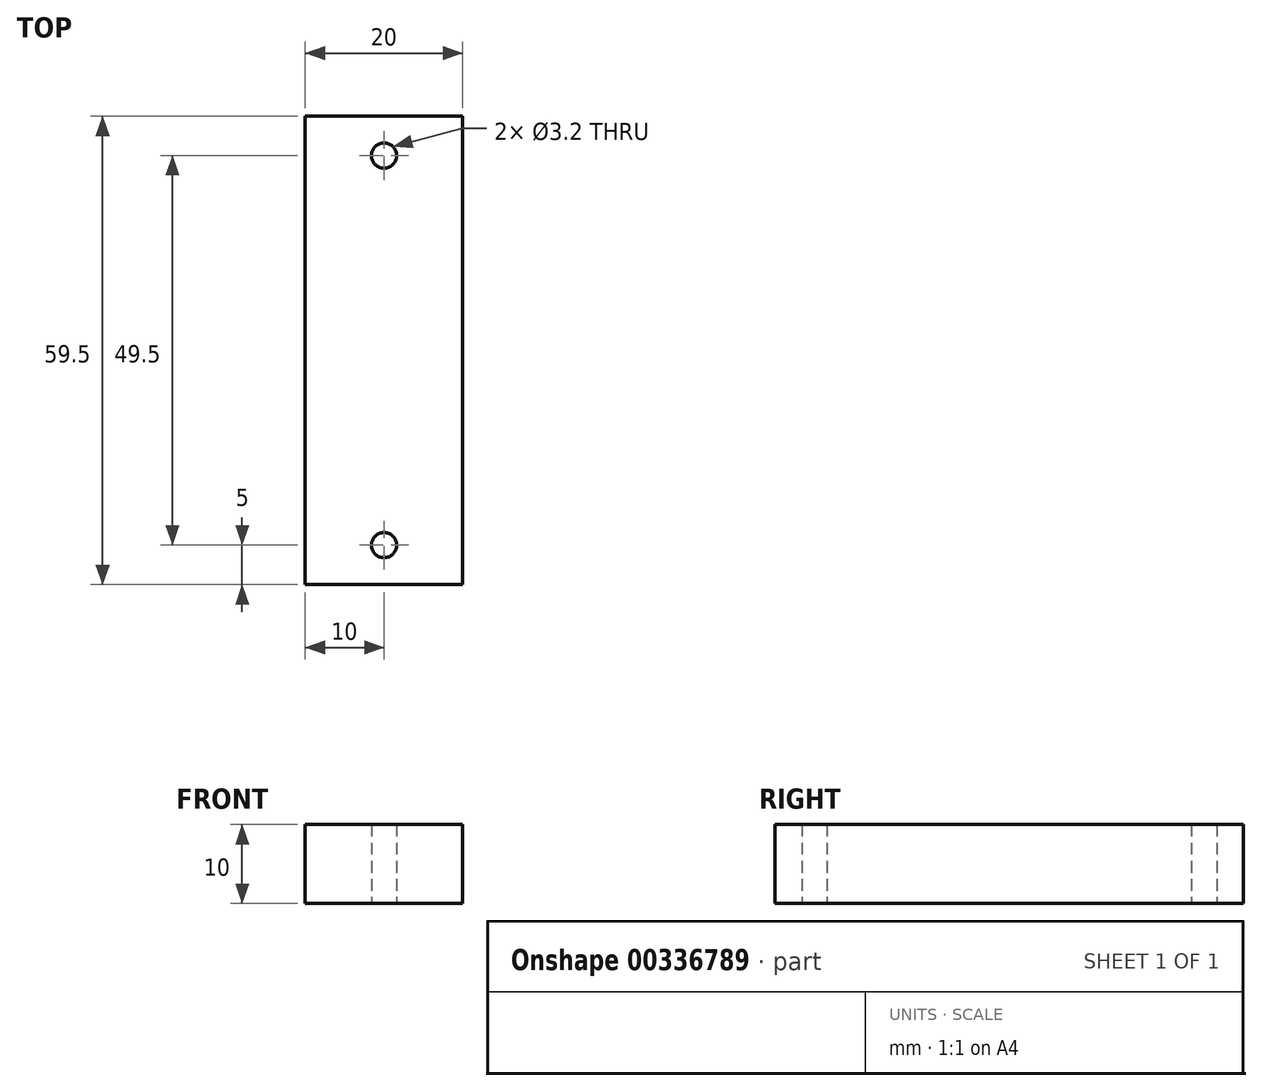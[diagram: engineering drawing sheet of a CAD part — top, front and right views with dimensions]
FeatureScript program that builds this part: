
annotation { "Feature Type Name" : "Feature", "Feature Type Description" : "" }
export const myFeature = defineFeature(function(context is Context, id is Id, definition is map)
    precondition{}
    {
        {
            var Q0;
            Q0=qCreatedBy(makeId("Top.planeOp"),FACE);
            var sketch = newSketch(context, id + "F0", { "sketchPlane" : qUnion([Q0])});
            skLineSegment(sketch, "E0.bottom", {"start": v(10, 29.75) * mm, "end": v(-10, 29.75) * mm});
            skLineSegment(sketch, "E0.top", {"start": v(10, -29.75) * mm, "end": v(-10, -29.75) * mm});
            skLineSegment(sketch, "E0.left", {"start": v(10, 29.75) * mm, "end": v(10, -29.75) * mm});
            skLineSegment(sketch, "E0.right", {"start": v(-10, 29.75) * mm, "end": v(-10, -29.75) * mm});
            skPoint(sketch, "E0.middle", {"position": v(0, 0) * mm});
            skPoint(sketch, "E1", {"position": v(0, 24.75) * mm});
            skCircle(sketch, "E2", {"center": v(0, 24.75) * mm, "radius": 1.6 * mm});
            skCircle(sketch, "E3.MirrorC", {"center": v(0, -24.75) * mm, "radius": 1.6 * mm});
            skSolve(sketch);
        }
        {
            var Q0;
            Q0=makeQuery(id+"F0.imprint","IMPRINT",FACE,{"disambiguationData":[TD([[makeQuery(id+"F0.imprint","IMPRINT",EDGE,{"derivedFrom":sQuery(id+"F0.wireOp",EDGE,"E0.bottom")}),1.0]])]});
            extrude(context, id + "F1", {"entities" : qUnion([Q0]), "depth" : 10 * mm});
        }
    });
